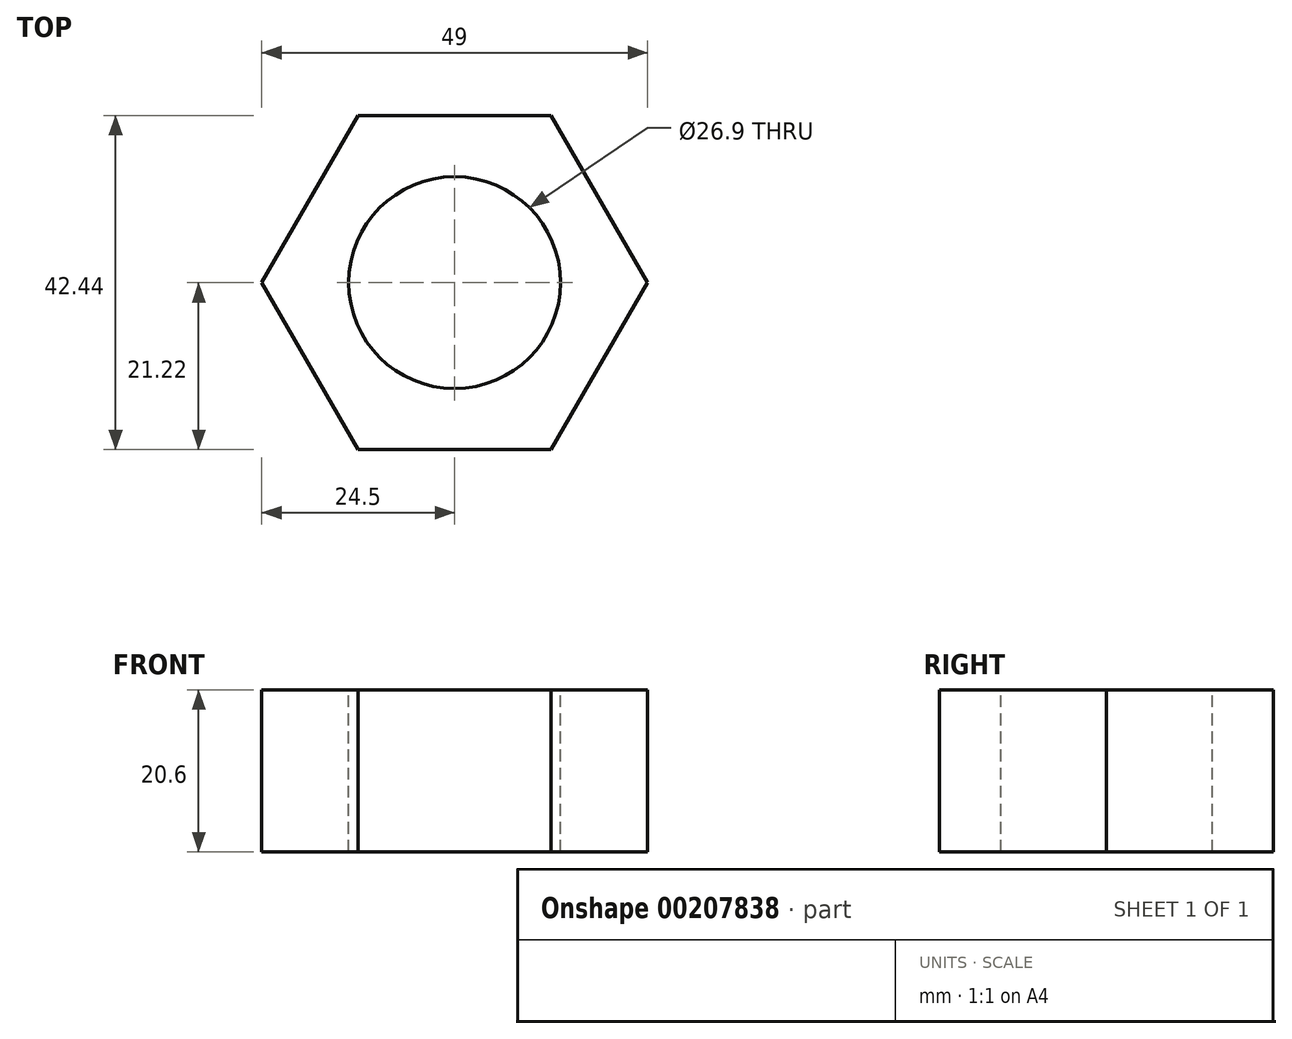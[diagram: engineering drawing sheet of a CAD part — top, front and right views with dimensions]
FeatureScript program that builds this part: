
annotation { "Feature Type Name" : "Feature", "Feature Type Description" : "" }
export const myFeature = defineFeature(function(context is Context, id is Id, definition is map)
    precondition{}
    {
        {
            var Q0;
            Q0=qCreatedBy(makeId("Top.planeOp"),FACE);
            var sketch = newSketch(context, id + "F0", { "sketchPlane" : qUnion([Q0])});
            skCircle(sketch, "E0.cCircle", {"center": v(0, 0) * mm, "radius": 24.5 * mm, "construction": true});
            skLineSegment(sketch, "E0.0", {"start": v(12.25, -21.22) * mm, "end": v(-12.25, -21.22) * mm});
            skLineSegment(sketch, "E0.1", {"start": v(-12.25, -21.22) * mm, "end": v(-24.5, 0) * mm});
            skLineSegment(sketch, "E0.2", {"start": v(-24.5, 0) * mm, "end": v(-12.25, 21.22) * mm});
            skLineSegment(sketch, "E0.3", {"start": v(-12.25, 21.22) * mm, "end": v(12.25, 21.22) * mm});
            skLineSegment(sketch, "E0.4", {"start": v(12.25, 21.22) * mm, "end": v(24.5, 0) * mm});
            skLineSegment(sketch, "E0.5", {"start": v(24.5, 0) * mm, "end": v(12.25, -21.22) * mm});
            skSolve(sketch);
        }
        {
            var Q0;
            Q0 = qSketchRegion(id + "F0", true);
            extrude(context, id + "F1", {"entities" : qUnion([Q0]), "depth" : 20.6 * mm});
        }
        {
            var Q0;
            Q0=makeQuery(id+"F1.opExtrude","CAP_FACE",FACE,{"disambiguationData":[OSD([sQuery(id+"F0.wireOp",EDGE,"E0.0"),sQuery(id+"F0.wireOp",EDGE,"E0.1"),sQuery(id+"F0.wireOp",EDGE,"E0.2"),sQuery(id+"F0.wireOp",EDGE,"E0.3"),sQuery(id+"F0.wireOp",EDGE,"E0.4"),sQuery(id+"F0.wireOp",EDGE,"E0.5")])],"isStart":false});
            var sketch = newSketch(context, id + "F2", { "sketchPlane" : qUnion([Q0])});
            skCircle(sketch, "E1", {"center": v(0, 0) * mm, "radius": 13.45 * mm});
            skSolve(sketch);
        }
        {
            var Q0;
            Q0 = qSketchRegion(id + "F2", true);
            extrude(context, id + "F3", {"entities" : qUnion([Q0]), "operationType" : NewBodyOperationType.ADD, "depth" : 25 * mm});
        }
        {
            var Q0;
            Q0=makeQuery(id+"F3.opExtrude","CAP_FACE",FACE,{"disambiguationData":[OSD([sQuery(id+"F2.wireOp",EDGE,"E1")])],"isStart":false});
            extrude(context, id + "F4", {"entities" : qUnion([Q0]), "operationType" : NewBodyOperationType.REMOVE, "endBound" : BoundingType.THROUGH_ALL, "oppositeDirection" : true, "depth" : 25 * mm});
        }
    });
